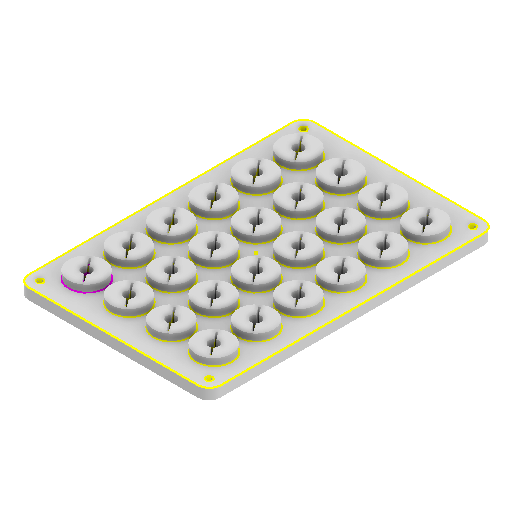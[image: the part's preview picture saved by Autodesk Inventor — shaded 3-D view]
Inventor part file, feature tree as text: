
AUTODESK INVENTOR PART (.ipt)
format: ipt  version: 2022 (Build 260153000, 153)  size: 653,824 bytes
history: native  units: mm
features: projected_geometry x17, sketch x7, extrude x4, hole x2, fillet x1, pattern_linear x1
ambient origin geometry x8: Origin, YZ Plane, XZ Plane, XY Plane, X Axis, Y Axis, Z Axis, Center Point
bodies: Volumenkörper1 (feature_tree)
feature tree (32):
  extrude  "Extrusion1"  Depth=127.5mm
  extrude  "Extrusion2"  Depth=5.0mm
  fillet  "Rundung1"  Radius=16.5mm
  hole  "Bohrung1"  [1 undecoded]
  extrude  "Extrusion3"  Depth=0.85mm
  pattern_linear  "Rechteckige Anordnung2"  Spacing1=0.85mm  [1 undecoded]
  extrude  "Extrusion4"  Depth=6.0mm TaperAngle=0.0deg
  hole  "Bohrung2"  [1 undecoded]
  sketch  "Skizze7"  dims[d25=13.2mm d26=0.85mm d27=6.0mm d28=0.0mm d29=60.0mm d31=18.9mm d32=40.0mm d34=18.9mm d35=13.2mm d36=21.816616mm d37=0.85mm d38=2.0mm d39=0.0mm d40=2.8mm d41=6.0mm d42=4.0mm d43=2.0mm d44=90.0deg d45=8.0mm d46=20.594885mm d30=0.375mm d33=20.594885mm]
  sketch  "Skizze1"  dims[d0=85.5mm d1=127.5mm]
  sketch  "Skizze2"  dims[d2=5.0mm d3=0.0mm d4=16.0mm d5=16.5mm]
  projected_geometry  "Projizierte Kontur1"
  sketch  "Skizze3"  dims[d6=14.4mm d7=3.0mm d8=0.0mm]
  projected_geometry  "Projizierte Kontur2"
  projected_geometry  "Projizierte Kontur3"
  sketch  "Skizze4"  dims[d15=0.85mm d16=13.0mm]
  projected_geometry  "Projizierte Kontur4"
  sketch  "Skizze5"  dims[d17=5.0mm]
  projected_geometry  "Projizierte Kontur5"
  sketch  "Skizze6"  dims[d18=4.6mm d19=6.0mm d20=4.0mm d21=2.0mm d22=90.0deg d23=0.01mm d24=20.594885mm]
  projected_geometry  "Projizierte Kontur6"
  projected_geometry  "Projizierte Kontur7"
  projected_geometry  "Projizierte Kontur8"
  projected_geometry  "Projizierte Kontur9"
  projected_geometry  "Projizierte Kontur10"
  projected_geometry  "Projizierte Kontur11"
  projected_geometry  "Projizierte Kontur12"
  projected_geometry  "Projizierte Kontur13"
  projected_geometry  "Projizierte Kontur14"
  projected_geometry  "Projizierte Kontur15"
  projected_geometry  "Projizierte Kontur16"
  projected_geometry  "Projizierte Kontur17"
note: 3 required parameter values undecoded (feature->parameter linkage not recoverable at this tier; creation-order binding heuristic only, values carry confidence <= 0.55)
